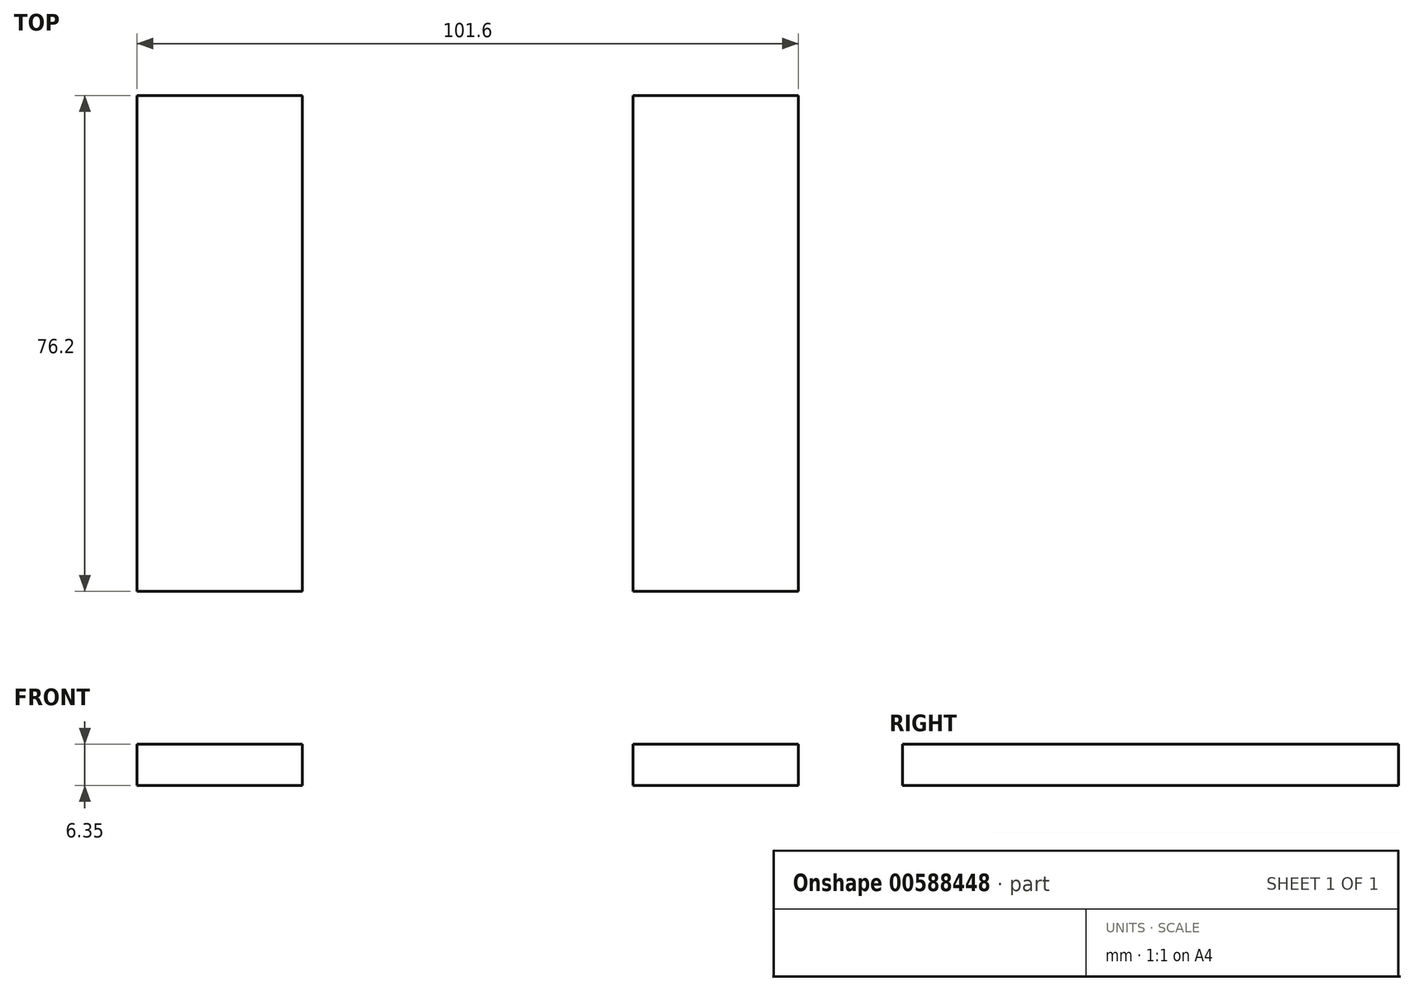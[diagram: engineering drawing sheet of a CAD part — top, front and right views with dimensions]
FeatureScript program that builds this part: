
annotation { "Feature Type Name" : "Feature", "Feature Type Description" : "" }
export const myFeature = defineFeature(function(context is Context, id is Id, definition is map)
    precondition{}
    {
        {
            var Q0;
            Q0=qCreatedBy(makeId("Top.planeOp"),FACE);
            var sketch = newSketch(context, id + "F0", { "sketchPlane" : qUnion([Q0])});
            skLineSegment(sketch, "E0.bottom", {"start": v(-50.8, -38.1) * mm, "end": v(-25.4, -38.1) * mm});
            skLineSegment(sketch, "E0.top", {"start": v(-50.8, 38.1) * mm, "end": v(-25.4, 38.1) * mm});
            skLineSegment(sketch, "E0.left", {"start": v(-50.8, -38.1) * mm, "end": v(-50.8, 38.1) * mm});
            skLineSegment(sketch, "E0.right", {"start": v(-25.4, -38.1) * mm, "end": v(-25.4, 38.1) * mm});
            skLineSegment(sketch, "E1.bottom", {"start": v(25.4, -38.1) * mm, "end": v(50.8, -38.1) * mm});
            skLineSegment(sketch, "E1.top", {"start": v(25.4, 38.1) * mm, "end": v(50.8, 38.1) * mm});
            skLineSegment(sketch, "E1.left", {"start": v(25.4, -38.1) * mm, "end": v(25.4, 38.1) * mm});
            skLineSegment(sketch, "E1.right", {"start": v(50.8, -38.1) * mm, "end": v(50.8, 38.1) * mm});
            skPoint(sketch, "E2.end.orphan", {"position": v(38.1, -38.1) * mm});
            skPoint(sketch, "E2.start.orphan", {"position": v(38.1, 38.1) * mm});
            skPoint(sketch, "E3.end.orphan", {"position": v(-38.1, -38.1) * mm});
            skPoint(sketch, "E3.start.orphan", {"position": v(-38.1, 38.1) * mm});
            skSolve(sketch);
        }
        {
            var Q0;
            Q0=makeQuery(id+"F0.imprint","IMPRINT",FACE,{"disambiguationData":[TD([[makeQuery(id+"F0.imprint","IMPRINT",EDGE,{"derivedFrom":sQuery(id+"F0.wireOp",EDGE,"E0.bottom")}),1.0]])]});
            var Q1;
            Q1=makeQuery(id+"F0.imprint","IMPRINT",FACE,{"disambiguationData":[TD([[makeQuery(id+"F0.imprint","IMPRINT",EDGE,{"derivedFrom":sQuery(id+"F0.wireOp",EDGE,"E1.bottom")}),1.0]])]});
            extrude(context, id + "F1", {"entities" : qUnion([Q0, Q1]), "oppositeDirection" : true, "depth" : 6.35 * mm, "offsetDistance" : 25.4 * mm});
        }
    });
